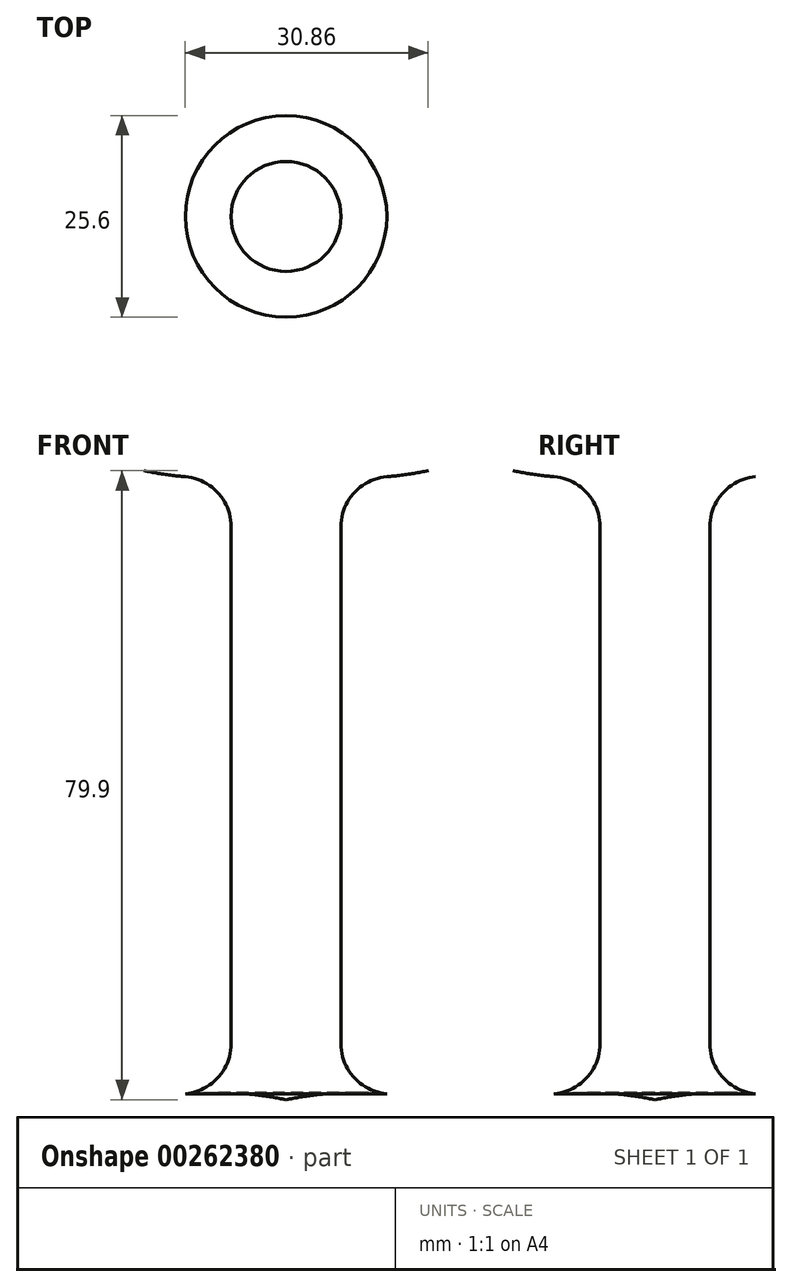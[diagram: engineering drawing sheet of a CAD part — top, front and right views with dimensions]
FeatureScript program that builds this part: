
annotation { "Feature Type Name" : "Feature", "Feature Type Description" : "" }
export const myFeature = defineFeature(function(context is Context, id is Id, definition is map)
    precondition{}
    {
        {
            var Q0;
            Q0=qCreatedBy(makeId("Front.planeOp"),FACE);
            var sketch = newSketch(context, id + "F0", { "sketchPlane" : qUnion([Q0])});
            skLineSegment(sketch, "E0", {"start": v(0, 127) * mm, "end": v(0, -127) * mm});
            skArc(sketch, "E1", {"start": v(12.8, 39.19) * mm, "mid": v(53.02, 89.89) * mm, "end": v(0, 127) * mm});
            skArc(sketch, "E2", {"start": v(0, -127) * mm, "mid": v(53.02, -89.89) * mm, "end": v(12.8, -39.19) * mm});
            skLineSegment(sketch, "E3", {"start": v(6.98, 32.86) * mm, "end": v(6.99, -32.86) * mm});
            skPoint(sketch, "E4.visualSharp", {"position": v(6.98, 39.07) * mm});
            skArc(sketch, "E4.filletArc", {"start": v(12.8, 39.19) * mm, "mid": v(8.66, 37.16) * mm, "end": v(6.98, 32.86) * mm});
            skPoint(sketch, "E5.visualSharp", {"position": v(6.99, -39.07) * mm});
            skArc(sketch, "E5.filletArc", {"start": v(6.98, -32.86) * mm, "mid": v(8.66, -37.16) * mm, "end": v(12.8, -39.19) * mm});
            skSolve(sketch);
        }
        {
            var Q0;
            Q0 = qSketchRegion(id + "F0", true);
            var Q1;
            Q1=sQuery(id+"F0.wireOp",EDGE,"E0");
            revolve(context, id + "F1", {"entities" : qUnion([Q0]), "axis" : qUnion([Q1]), "revolveType" : RevolveType.FULL});
        }
        {
            var Q0;
            Q0=qCreatedBy(makeId("Top.planeOp"),FACE);
            var sketch = newSketch(context, id + "F2", { "sketchPlane" : qUnion([Q0])});
            skLineSegment(sketch, "E6.bottom", {"start": v(-84.12, -51.82) * mm, "end": v(-44.45, -51.82) * mm});
            skLineSegment(sketch, "E6.top", {"start": v(-84.12, 69.43) * mm, "end": v(-44.45, 69.43) * mm});
            skLineSegment(sketch, "E6.left", {"start": v(-84.12, -51.82) * mm, "end": v(-84.12, 69.43) * mm});
            skLineSegment(sketch, "E6.right", {"start": v(-44.45, -51.82) * mm, "end": v(-44.45, 69.43) * mm});
            skSolve(sketch);
        }
        {
            var Q0;
            Q0 = qSketchRegion(id + "F2", true);
            extrude(context, id + "F3", {"entities" : qUnion([Q0]), "operationType" : NewBodyOperationType.REMOVE, "endBound" : BoundingType.SYMMETRIC, "oppositeDirection" : true, "depth" : 254 * mm});
        }
    });
